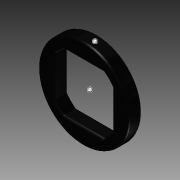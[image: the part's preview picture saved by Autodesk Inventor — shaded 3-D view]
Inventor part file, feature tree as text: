
AUTODESK INVENTOR PART (.ipt)
format: ipt  version: 2015 (Build 190159000, 159)  size: 223,744 bytes
history: native  units: in
note: dims shown in document units (in); Inventor stores cm internally (conversion verified against a paired STEP export)
features: fillet x1, other x1, imported_body x1
ambient origin geometry x8: Origin, YZ Plane, XZ Plane, XY Plane, X Axis, Y Axis, Z Axis, Center Point
bodies: Body1 (feature_tree)
feature tree (3):
  fillet  "Fillet1"  [1 undecoded]
  other  "Spacer HS 0.125 unit"
  imported_body  "Base1"
note: 1 required parameter value undecoded (feature->parameter linkage not recoverable at this tier; creation-order binding heuristic only, values carry confidence <= 0.55)
